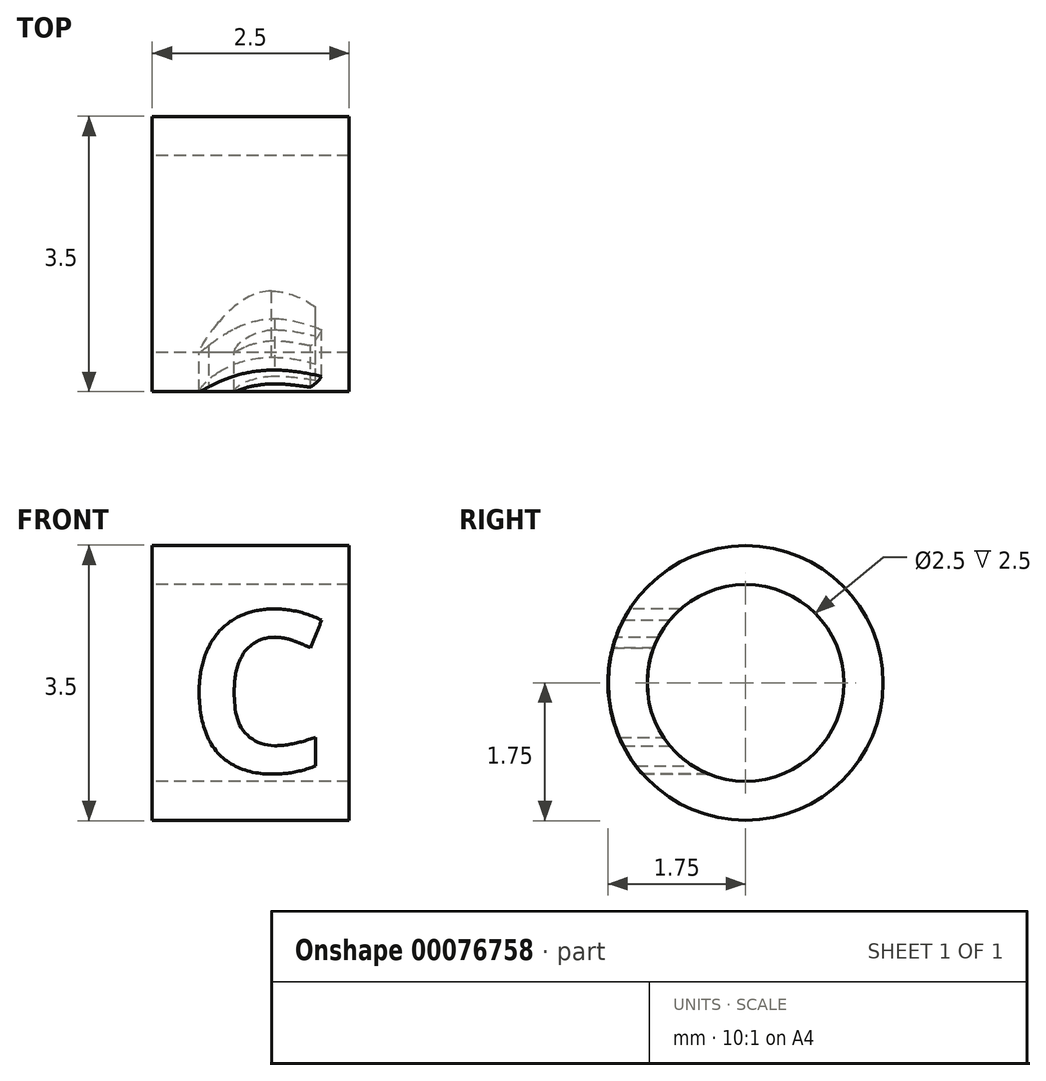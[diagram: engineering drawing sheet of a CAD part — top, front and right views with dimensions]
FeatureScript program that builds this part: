
annotation { "Feature Type Name" : "Feature", "Feature Type Description" : "" }
export const myFeature = defineFeature(function(context is Context, id is Id, definition is map)
    precondition{}
    {
        {
            var Q0;
            Q0=qCreatedBy(makeId("Right.planeOp"),FACE);
            var sketch = newSketch(context, id + "F0", { "sketchPlane" : qUnion([Q0])});
            skCircle(sketch, "E0", {"center": v(0, 0) * mm, "radius": 1.25 * mm});
            skCircle(sketch, "E1", {"center": v(0, 0) * mm, "radius": 1.75 * mm});
            skSolve(sketch);
        }
        {
            var Q0;
            Q0=makeQuery(id+"F0.imprint","IMPRINT",FACE,{"disambiguationData":[TD([[makeQuery(id+"F0.imprint","IMPRINT",EDGE,{"derivedFrom":sQuery(id+"F0.wireOp",EDGE,"E0")}),-1.0]])]});
            var Q1;
            Q1=makeQuery(id+"F0.imprint","IMPRINT",FACE,{"disambiguationData":[TD([[makeQuery(id+"F0.imprint","IMPRINT",EDGE,{"derivedFrom":sQuery(id+"F0.wireOp",EDGE,"E1")}),1.0]])]});
            extrude(context, id + "F1", {"entities" : qUnion([Q0, Q1]), "depth" : 2.5 * mm});
        }
        {
            var Q0;
            Q0=qCreatedBy(makeId("Front.planeOp"),FACE);
            var sketch = newSketch(context, id + "F2", { "sketchPlane" : qUnion([Q0])});
            skText(sketch, "E2", { "text": "C", "fontName": "OpenSans-Bold.ttf"});
            const initialGuessF2  = {"E2": [0.00043, -0.00113, 1, 0, 0.00206]};
            skSetInitialGuess(sketch, initialGuessF2);
            skSolve(sketch);
        }
        {
            var Q0;
            Q0=qSketchRegion(id+"F2",true);
            var Q1;
            Q1=qConstructionFilter(qBodyType(qCreatedBy(id+"F2",EDGE),BodyType.WIRE),ConstructionObject.NO);
            var Q2;
            Q2=makeQuery(id+"F1.opExtrude","SWEPT_FACE",FACE,{"disambiguationData":[OSD([sQuery(id+"F0.wireOp",EDGE,"E1")])]});
            var Q3;
            Q3=makeQuery(id+"F1.opExtrude","SWEPT_BODY",BODY,{"disambiguationData":[OSD([sQuery(id+"F0.wireOp",EDGE,"E0"),sQuery(id+"F0.wireOp",EDGE,"E1")])]});
            var Q4;
            Q4=sQuery(id+"F0.wireOp",VERTEX,"27635d6e-dcd6-4653-b727-4819003c0945");
            extrude(context, id + "F3", {"entities" : qUnion([Q0]), "operationType" : NewBodyOperationType.INTERSECT, "surfaceEntities" : qUnion([Q1]), "endBound" : BoundingType.UP_TO_SURFACE, "endBoundEntityFace" : qUnion([Q2]), "endBoundEntityBody" : qUnion([Q3]), "endBoundEntityVertex" : qUnion([Q4]), "depth" : 25 * mm});
        }
        {
            var Q0;
            Q0=makeQuery(id+"F0.imprint","IMPRINT",FACE,{"disambiguationData":[TD([[makeQuery(id+"F0.imprint","IMPRINT",EDGE,{"derivedFrom":sQuery(id+"F0.wireOp",EDGE,"E0")}),-1.0]])]});
            extrude(context, id + "F4", {"entities" : qUnion([Q0]), "depth" : 2.5 * mm});
        }
    });
